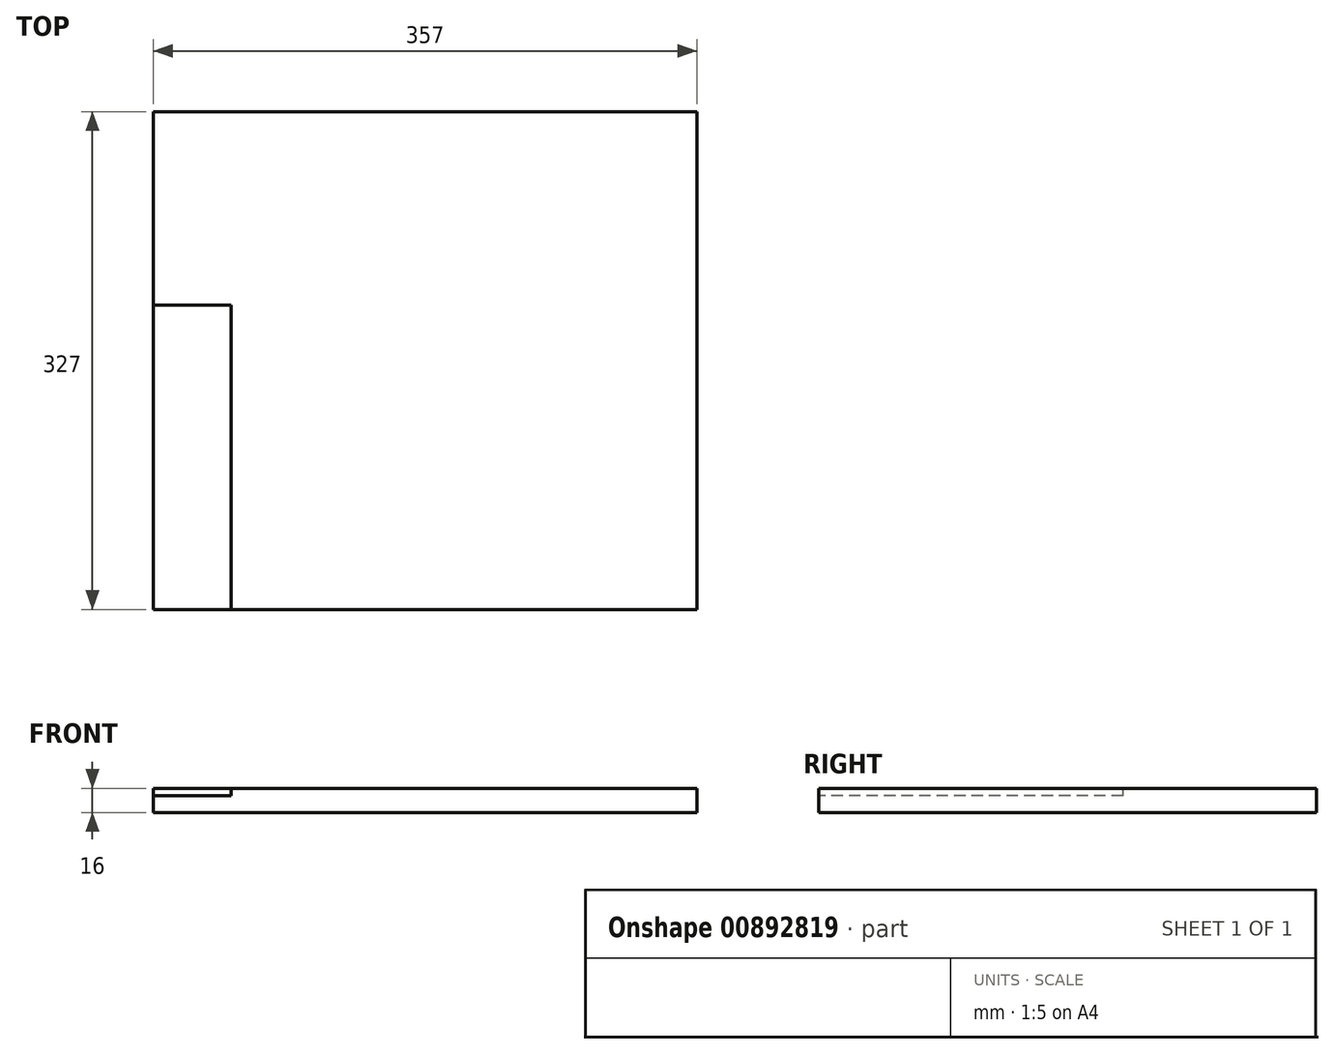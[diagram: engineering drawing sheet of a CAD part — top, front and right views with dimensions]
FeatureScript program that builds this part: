
annotation { "Feature Type Name" : "Feature", "Feature Type Description" : "" }
export const myFeature = defineFeature(function(context is Context, id is Id, definition is map)
    precondition{}
    {
        {
            var Q0;
            Q0=qCreatedBy(makeId("Top.planeOp"),FACE);
            var sketch = newSketch(context, id + "F0", { "sketchPlane" : qUnion([Q0])});
            skLineSegment(sketch, "E0.bottom", {"start": v(-178.5, 163.5) * mm, "end": v(178.5, 163.5) * mm});
            skLineSegment(sketch, "E0.top", {"start": v(-178.5, -163.5) * mm, "end": v(178.5, -163.5) * mm});
            skLineSegment(sketch, "E0.left", {"start": v(-178.5, 163.5) * mm, "end": v(-178.5, -163.5) * mm});
            skLineSegment(sketch, "E0.right", {"start": v(178.5, 163.5) * mm, "end": v(178.5, -163.5) * mm});
            skLineSegment(sketch, "E1", {"start": v(0, 93.5) * mm, "end": v(0, -93.5) * mm, "construction": true});
            skLineSegment(sketch, "E2", {"start": v(-97.82, 0) * mm, "end": v(97.82, 0) * mm, "construction": true});
            skSolve(sketch);
        }
        {
            var Q0;
            Q0 = qSketchRegion(id + "F0", true);
            extrude(context, id + "F1", {"entities" : qUnion([Q0]), "depth" : 16 * mm, "offsetDistance" : 25 * mm});
        }
        {
            var Q0;
            Q0=makeQuery(id+"F1.opExtrude","CAP_FACE",FACE,{"disambiguationData":[OSD([sQuery(id+"F0.wireOp",EDGE,"E0.bottom"),sQuery(id+"F0.wireOp",EDGE,"E0.top"),sQuery(id+"F0.wireOp",EDGE,"E0.left"),sQuery(id+"F0.wireOp",EDGE,"E0.right")])],"isStart":false});
            var sketch = newSketch(context, id + "F2", { "sketchPlane" : qUnion([Q0])});
            skLineSegment(sketch, "E3.bottom", {"start": v(-178.5, -163.5) * mm, "end": v(-127.5, -163.5) * mm});
            skLineSegment(sketch, "E3.top", {"start": v(-178.5, 36.5) * mm, "end": v(-127.5, 36.5) * mm});
            skLineSegment(sketch, "E3.left", {"start": v(-178.5, -163.5) * mm, "end": v(-178.5, 36.5) * mm});
            skLineSegment(sketch, "E3.right", {"start": v(-127.5, -163.5) * mm, "end": v(-127.5, 36.5) * mm});
            skSolve(sketch);
        }
        {
            var Q0;
            Q0=makeQuery(id+"F2.imprint","IMPRINT",FACE,{"disambiguationData":[TD([[makeQuery(id+"F2.imprint","IMPRINT",EDGE,{"derivedFrom":sQuery(id+"F2.wireOp",EDGE,"E3.bottom")}),1.0]])]});
            extrude(context, id + "F3", {"entities" : qUnion([Q0]), "operationType" : NewBodyOperationType.REMOVE, "oppositeDirection" : true, "depth" : 5 * mm, "offsetDistance" : 25 * mm});
        }
    });
